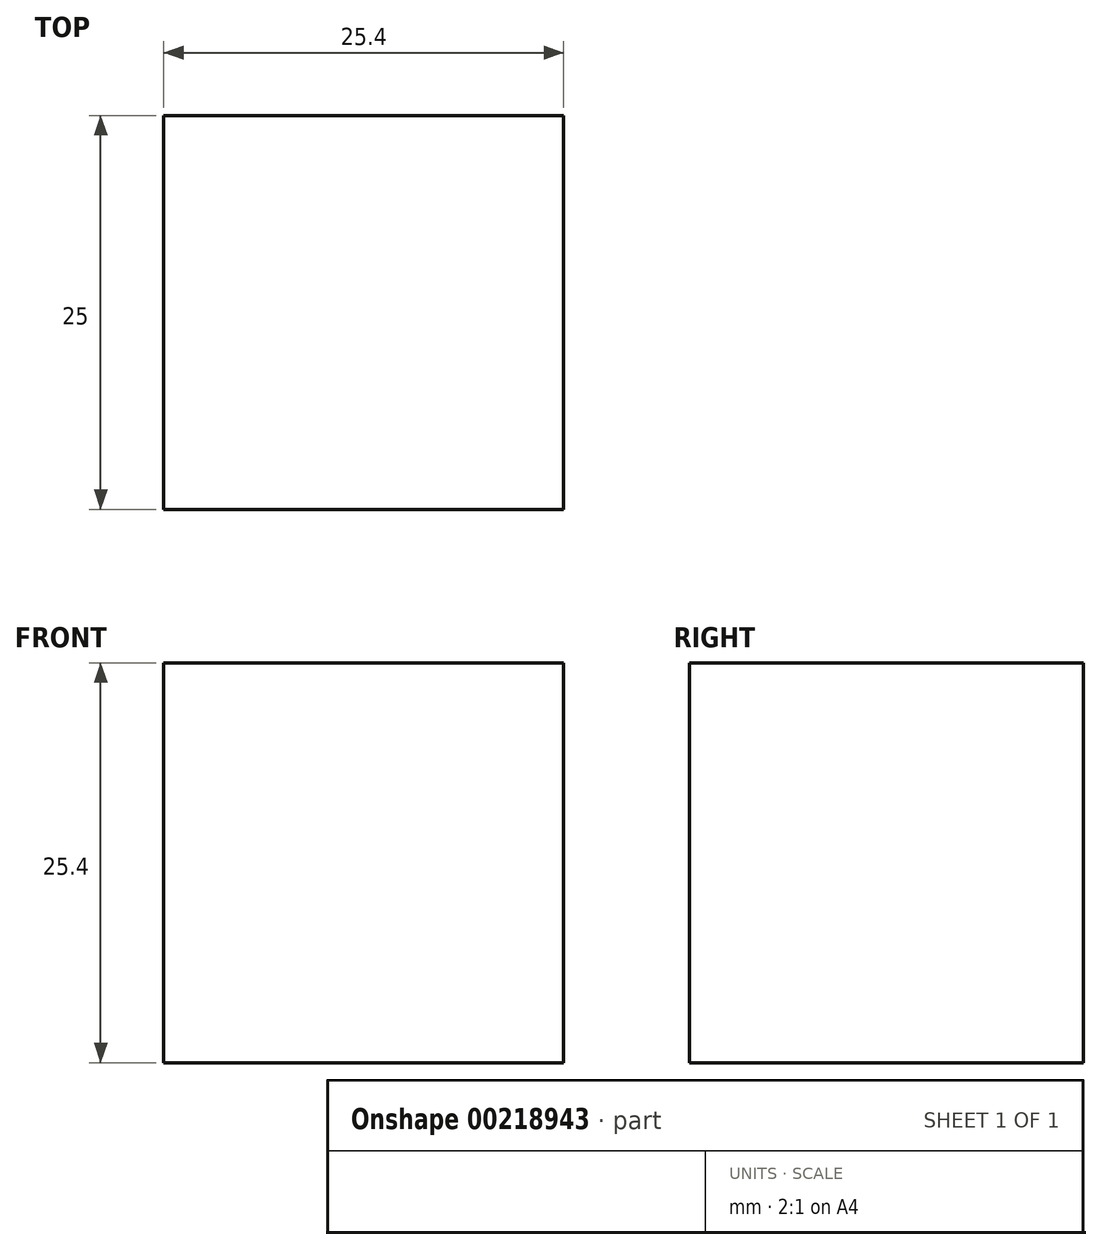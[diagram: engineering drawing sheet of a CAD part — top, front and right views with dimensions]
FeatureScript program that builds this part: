
annotation { "Feature Type Name" : "Feature", "Feature Type Description" : "" }
export const myFeature = defineFeature(function(context is Context, id is Id, definition is map)
    precondition{}
    {
        {
            var Q0;
            Q0=qCreatedBy(makeId("Front.planeOp"),FACE);
            var sketch = newSketch(context, id + "F0", { "sketchPlane" : qUnion([Q0])});
            skLineSegment(sketch, "E0.bottom", {"start": v(12.7, -12.7) * mm, "end": v(-12.7, -12.7) * mm});
            skLineSegment(sketch, "E0.top", {"start": v(12.7, 12.7) * mm, "end": v(-12.7, 12.7) * mm});
            skLineSegment(sketch, "E0.left", {"start": v(12.7, -12.7) * mm, "end": v(12.7, 12.7) * mm});
            skLineSegment(sketch, "E0.right", {"start": v(-12.7, -12.7) * mm, "end": v(-12.7, 12.7) * mm});
            skPoint(sketch, "E0.middle", {"position": v(0, 0) * mm});
            skSolve(sketch);
        }
        {
            var Q0;
            Q0=makeQuery(id+"F0.imprint","IMPRINT",FACE,{"disambiguationData":[TD([[makeQuery(id+"F0.imprint","IMPRINT",EDGE,{"derivedFrom":sQuery(id+"F0.wireOp",EDGE,"E0.bottom")}),-1.0]])]});
            extrude(context, id + "F1", {"entities" : qUnion([Q0]), "depth" : 25 * mm});
        }
    });
